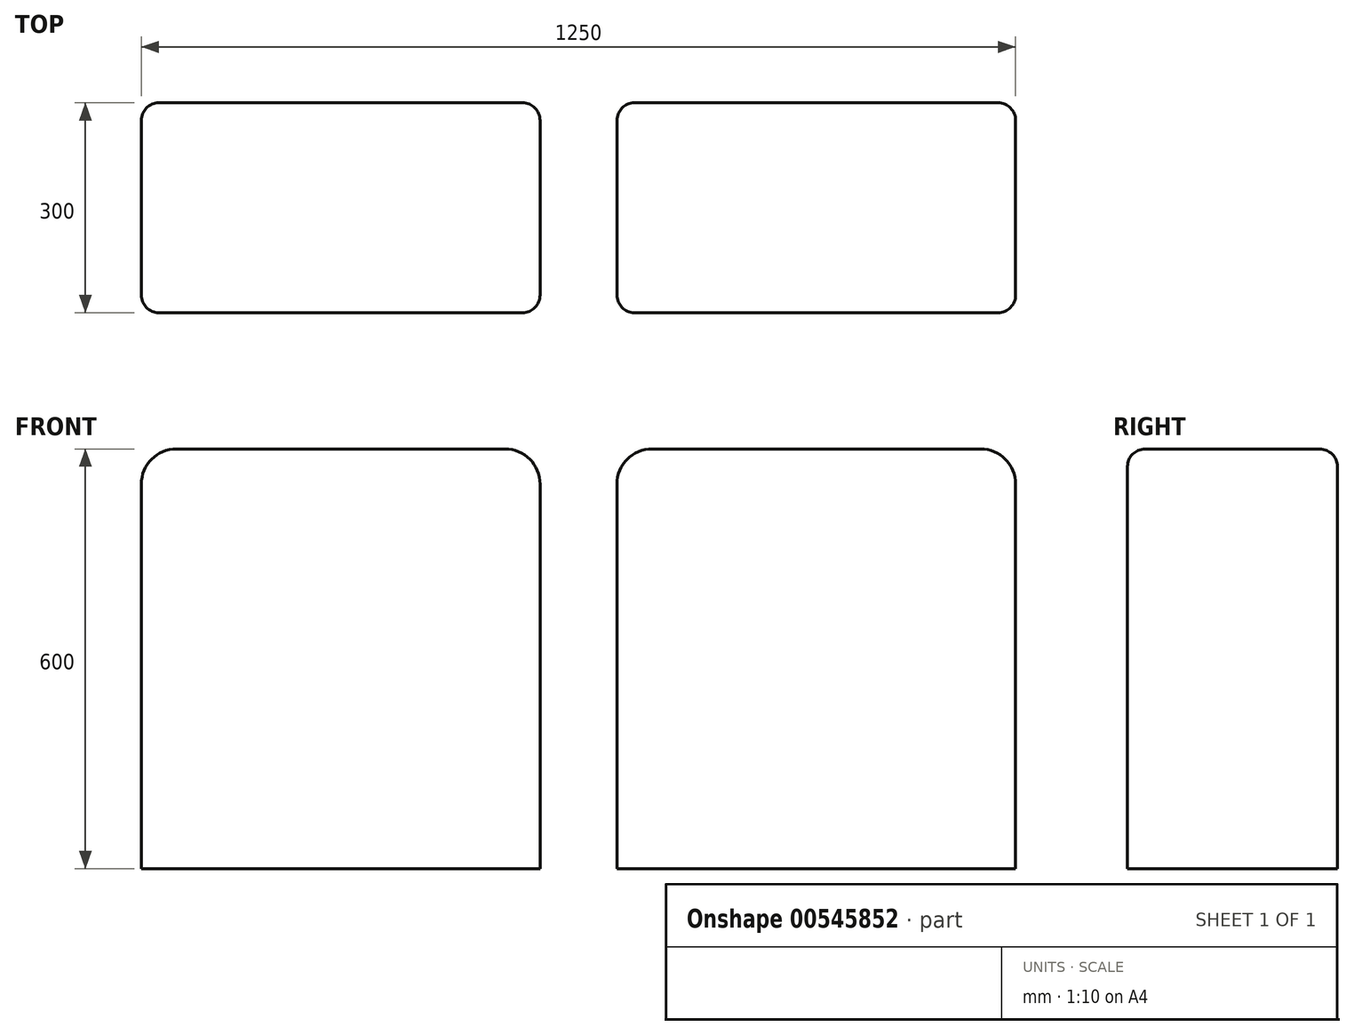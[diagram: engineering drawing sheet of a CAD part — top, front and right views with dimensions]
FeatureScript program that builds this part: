
annotation { "Feature Type Name" : "Feature", "Feature Type Description" : "" }
export const myFeature = defineFeature(function(context is Context, id is Id, definition is map)
    precondition{}
    {
        {
            var Q0;
            Q0=qCreatedBy(makeId("Top.planeOp"),FACE);
            var sketch = newSketch(context, id + "F0", { "sketchPlane" : qUnion([Q0])});
            skLineSegment(sketch, "E0", {"start": v(0, 0) * mm, "end": v(0, -1700) * mm, "construction": true});
            skLineSegment(sketch, "E1", {"start": v(0, -1700) * mm, "end": v(-425, -1700) * mm, "construction": true});
            skLineSegment(sketch, "E2", {"start": v(-675, 0) * mm, "end": v(0, 0) * mm, "construction": true});
            skLineSegment(sketch, "E3", {"start": v(-675, -1200) * mm, "end": v(-675, -1700) * mm, "construction": true});
            skLineSegment(sketch, "E4", {"start": v(-675, -1700) * mm, "end": v(-425, -1700) * mm, "construction": true});
            skLineSegment(sketch, "E5.MirrorCS", {"start": v(0, -1700) * mm, "end": v(425, -1700) * mm, "construction": true});
            skLineSegment(sketch, "E6", {"start": v(-425, -1700) * mm, "end": v(-675, -1200) * mm, "construction": true});
            skLineSegment(sketch, "E7", {"start": v(425, -1700) * mm, "end": v(-425, -1700) * mm});
            skLineSegment(sketch, "E8", {"start": v(675, -1200) * mm, "end": v(425, -1700) * mm, "construction": true});
            skLineSegment(sketch, "E9", {"start": v(-675, -1200) * mm, "end": v(-675, 0) * mm, "construction": true});
            skLineSegment(sketch, "E10", {"start": v(-675, -1200) * mm, "end": v(-675, -1700) * mm});
            skLineSegment(sketch, "E11", {"start": v(-425, -1700) * mm, "end": v(-425, -1200) * mm});
            skLineSegment(sketch, "E12", {"start": v(-425, -1200) * mm, "end": v(-675, -1200) * mm});
            skLineSegment(sketch, "E13.MirrorCS", {"start": v(425, -1200) * mm, "end": v(675, -1200) * mm});
            skLineSegment(sketch, "E14.MirrorCS", {"start": v(425, -1700) * mm, "end": v(425, -1200) * mm});
            skLineSegment(sketch, "E15.MirrorCS", {"start": v(675, -1700) * mm, "end": v(425, -1700) * mm, "construction": true});
            skLineSegment(sketch, "E16.MirrorCS", {"start": v(675, -1200) * mm, "end": v(675, -1700) * mm, "construction": true});
            skLineSegment(sketch, "E17", {"start": v(-675, -650) * mm, "end": v(675, -650) * mm, "construction": true});
            skLineSegment(sketch, "E18.bottom", {"start": v(-675, 0) * mm, "end": v(675, 0) * mm});
            skLineSegment(sketch, "E18.left", {"start": v(-675, 0) * mm, "end": v(-675, 0) * mm});
            skLineSegment(sketch, "E18.right", {"start": v(675, 0) * mm, "end": v(675, -1700) * mm});
            skLineSegment(sketch, "E19.bottom", {"start": v(-625, -180) * mm, "end": v(-55, -180) * mm});
            skLineSegment(sketch, "E19.top", {"start": v(-625, -480) * mm, "end": v(-55, -480) * mm});
            skLineSegment(sketch, "E19.left", {"start": v(-625, -180) * mm, "end": v(-625, -480) * mm});
            skLineSegment(sketch, "E19.right", {"start": v(-55, -180) * mm, "end": v(-55, -480) * mm});
            skSolve(sketch);
        }
        {
            var Q0;
            Q0=makeQuery(id+"F0.imprint","IMPRINT",FACE,{"disambiguationData":[TD([[makeQuery(id+"F0.imprint","IMPRINT",EDGE,{"derivedFrom":sQuery(id+"F0.wireOp",EDGE,"E19.bottom")}),-1.0]])]});
            extrude(context, id + "F1", {"entities" : qUnion([Q0]), "depth" : 600 * mm, "offsetDistance" : 25 * mm});
        }
        {
            var Q0;
            Q0=makeQuery(id+"F1.opExtrude","CAP_EDGE",EDGE,{"disambiguationData":[OSD([sQuery(id+"F0.wireOp",EDGE,"E19.left")])],"isStart":false});
            var Q1;
            Q1=makeQuery(id+"F1.opExtrude","CAP_EDGE",EDGE,{"disambiguationData":[OSD([sQuery(id+"F0.wireOp",EDGE,"E19.right")])],"isStart":false});
            fillet(context, id + "F2", {"entities" : qUnion([Q0, Q1]), "radius" : 50 * mm, "tangentPropagation" : true, "allowEdgeOverflow" : false});
        }
        {
            var Q0;
            Q0=makeQuery(id+"F1.opExtrude","SWEPT_EDGE",EDGE,{"disambiguationData":[OSD([sQuery(id+"F0.wireOp",EDGE,"E19.top"),sQuery(id+"F0.wireOp",EDGE,"E19.left")])]});
            var Q1;
            Q1=makeQuery(id+"F1.opExtrude","CAP_EDGE",EDGE,{"disambiguationData":[OSD([sQuery(id+"F0.wireOp",EDGE,"E19.top")])],"isStart":false});
            var Q2;
            Q2=makeQuery(id+"F1.opExtrude","SWEPT_EDGE",EDGE,{"disambiguationData":[OSD([sQuery(id+"F0.wireOp",EDGE,"E19.top"),sQuery(id+"F0.wireOp",EDGE,"E19.right")])]});
            var Q3;
            Q3=makeQuery(id+"F1.opExtrude","SWEPT_EDGE",EDGE,{"disambiguationData":[OSD([sQuery(id+"F0.wireOp",EDGE,"E19.bottom"),sQuery(id+"F0.wireOp",EDGE,"E19.right")])]});
            fillet(context, id + "F3", {"entities" : qUnion([Q0, Q1, Q2, Q3]), "radius" : 25 * mm, "tangentPropagation" : true, "allowEdgeOverflow" : false});
        }
        {
            var Q0;
            Q0=makeQuery(id+"F1.opExtrude","SWEPT_BODY",BODY,{"disambiguationData":[OSD([sQuery(id+"F0.wireOp",EDGE,"E19.bottom"),sQuery(id+"F0.wireOp",EDGE,"E19.top"),sQuery(id+"F0.wireOp",EDGE,"E19.left"),sQuery(id+"F0.wireOp",EDGE,"E19.right")])]});
            var Q1;
            Q1=qCreatedBy(makeId("Right.planeOp"),FACE);
            mirror(context, id + "F4", {"entities" : qUnion([Q0]), "mirrorPlane" : qUnion([Q1])});
        }
    });
